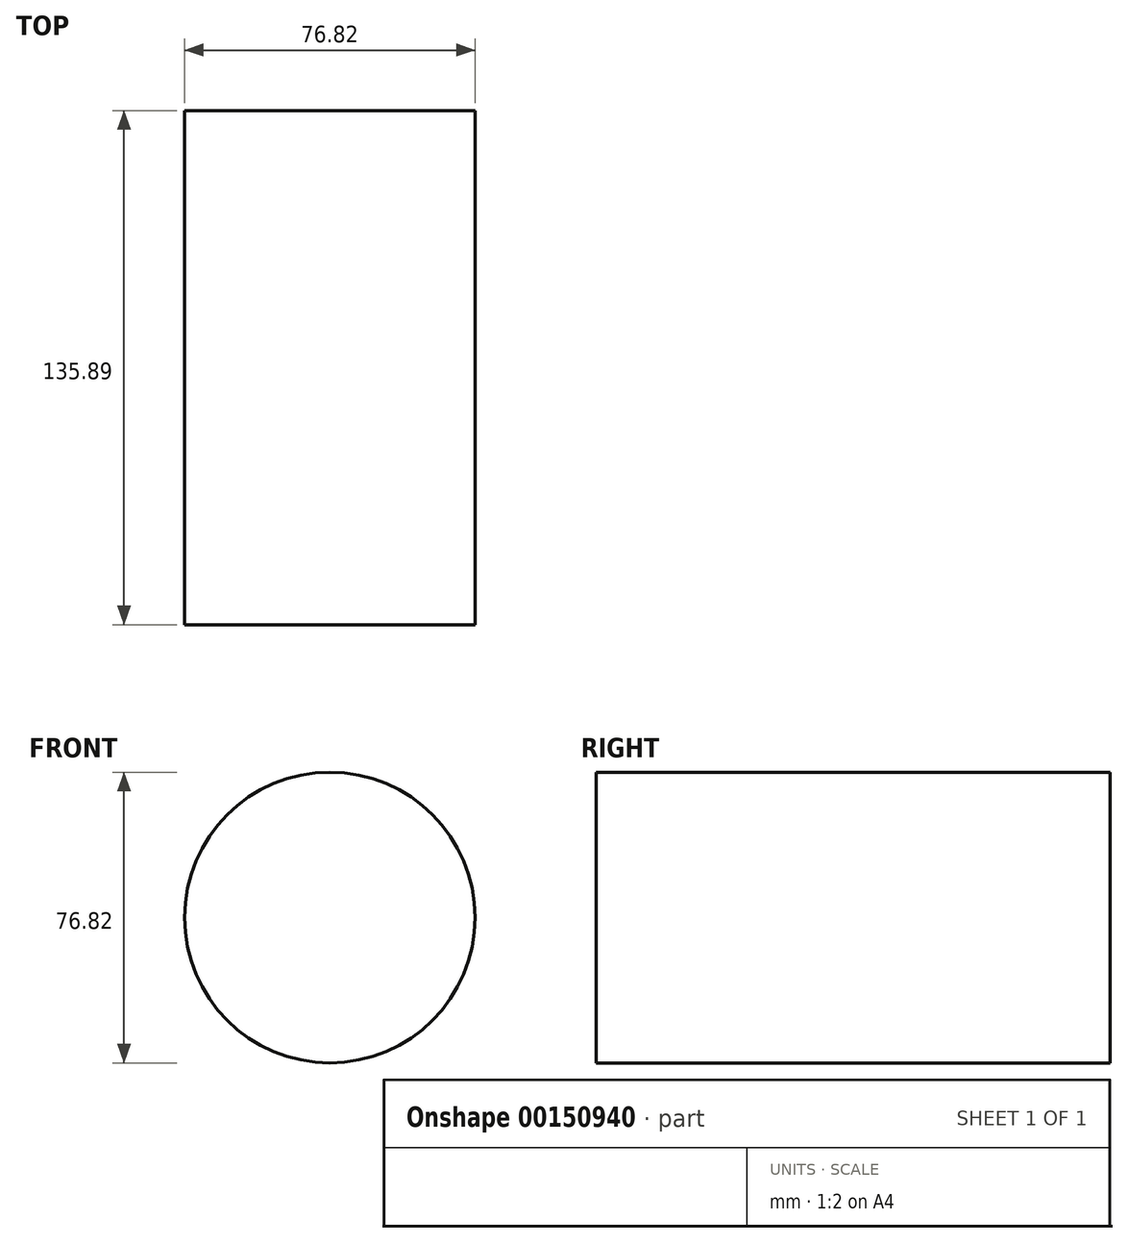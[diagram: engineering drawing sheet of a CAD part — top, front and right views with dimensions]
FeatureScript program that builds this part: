
annotation { "Feature Type Name" : "Feature", "Feature Type Description" : "" }
export const myFeature = defineFeature(function(context is Context, id is Id, definition is map)
    precondition{}
    {
        {
            var Q0;
            Q0=qCreatedBy(makeId("Front.planeOp"),FACE);
            var sketch = newSketch(context, id + "F0", { "sketchPlane" : qUnion([Q0])});
            skCircle(sketch, "E0", {"center": v(0, 0) * mm, "radius": 38.4 * mm});
            skSolve(sketch);
        }
        {
            var Q0;
            Q0=qCreatedBy(makeId("Top.planeOp"),FACE);
            var sketch = newSketch(context, id + "F1", { "sketchPlane" : qUnion([Q0])});
            skLineSegment(sketch, "E1.bottom", {"start": v(63.5, -38.1) * mm, "end": v(-63.5, -38.1) * mm});
            skLineSegment(sketch, "E1.top", {"start": v(63.5, 38.1) * mm, "end": v(-63.5, 38.1) * mm});
            skLineSegment(sketch, "E1.left", {"start": v(63.5, -38.1) * mm, "end": v(63.5, 38.1) * mm});
            skLineSegment(sketch, "E1.right", {"start": v(-63.5, -38.1) * mm, "end": v(-63.5, 38.1) * mm});
            skPoint(sketch, "E1.middle", {"position": v(0, 0) * mm});
            skSolve(sketch);
        }
        {
            var Q0;
            Q0 = qSketchRegion(id + "F1", true);
            extrude(context, id + "F2", {"entities" : qUnion([Q0]), "depth" : 25.4 * mm});
        }
        {
            var Q0;
            Q0=makeQuery(id+"F2.opExtrude","SWEPT_BODY",BODY,{"disambiguationData":[OSD([sQuery(id+"F1.wireOp",EDGE,"E1.bottom"),sQuery(id+"F1.wireOp",EDGE,"E1.top"),sQuery(id+"F1.wireOp",EDGE,"E1.left"),sQuery(id+"F1.wireOp",EDGE,"E1.right")])]});
            deleteBodies(context, id + "F3", {"entities" : qUnion([Q0])});
        }
        {
            var Q0;
            Q0=makeQuery(id+"F0.imprint","IMPRINT",FACE,{"disambiguationData":[TD([[makeQuery(id+"F0.imprint","IMPRINT",EDGE,{"derivedFrom":sQuery(id+"F0.wireOp",EDGE,"E0")}),1.0]])]});
            extrude(context, id + "F4", {"entities" : qUnion([Q0]), "oppositeDirection" : true, "depth" : 135.89 * mm});
        }
    });
